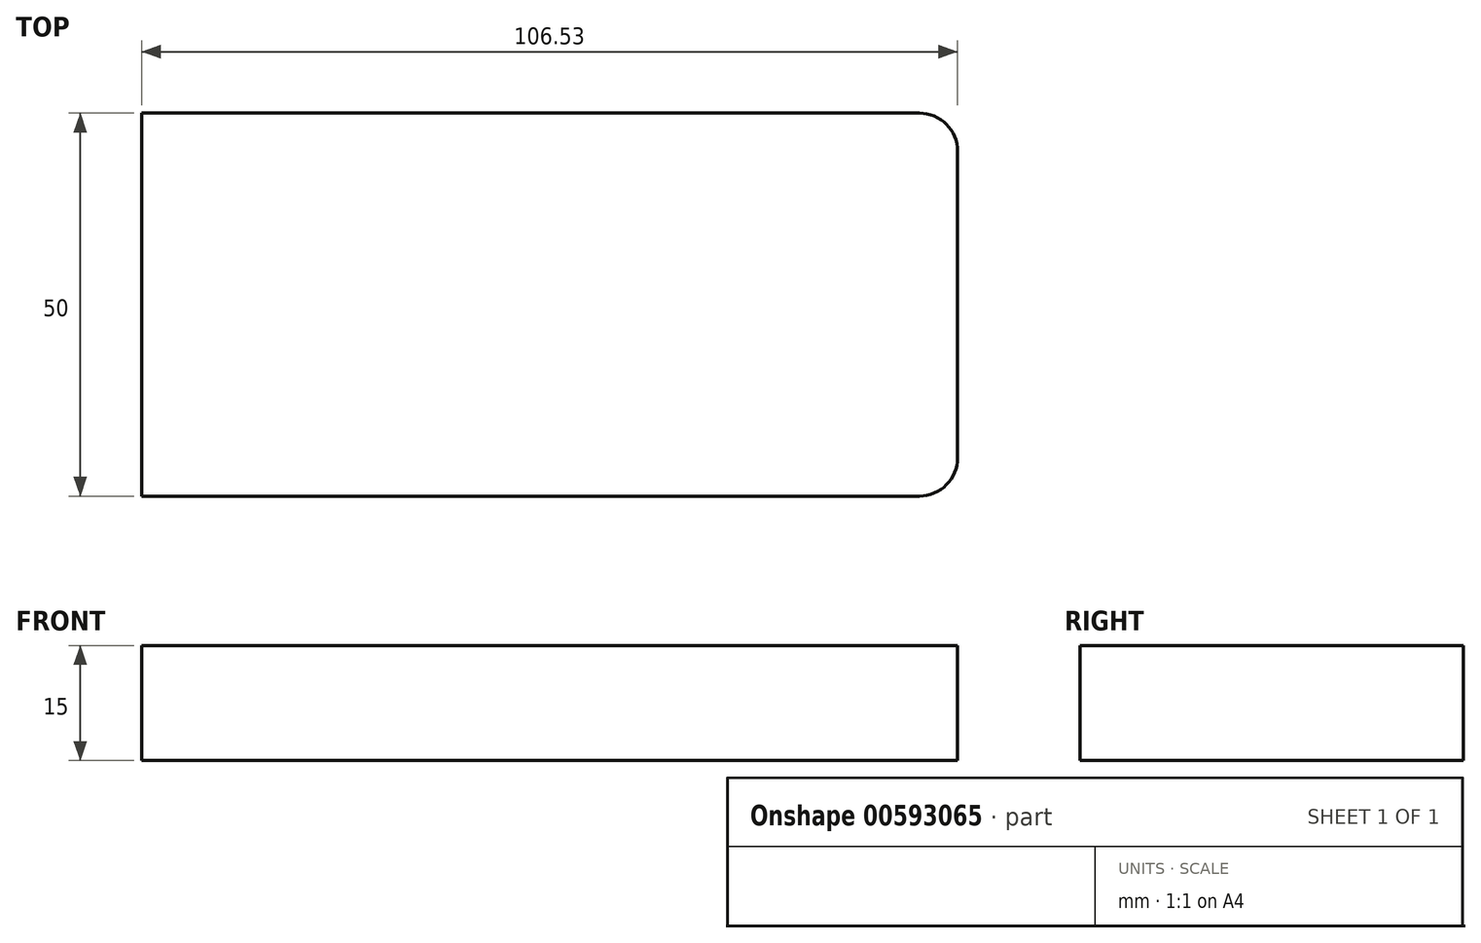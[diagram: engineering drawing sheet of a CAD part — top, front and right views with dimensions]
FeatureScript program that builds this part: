
annotation { "Feature Type Name" : "Feature", "Feature Type Description" : "" }
export const myFeature = defineFeature(function(context is Context, id is Id, definition is map)
    precondition{}
    {
        {
            var Q0;
            Q0=qCreatedBy(makeId("Top.planeOp"),FACE);
            var sketch = newSketch(context, id + "F0", { "sketchPlane" : qUnion([Q0])});
            skLineSegment(sketch, "E0.bottom", {"start": v(0, 0) * mm, "end": v(101.53, 0) * mm});
            skLineSegment(sketch, "E0.top", {"start": v(0, -50) * mm, "end": v(101.53, -50) * mm});
            skLineSegment(sketch, "E0.left", {"start": v(0, 0) * mm, "end": v(0, -50) * mm});
            skLineSegment(sketch, "E0.right", {"start": v(106.53, -5) * mm, "end": v(106.53, -45) * mm});
            skPoint(sketch, "E1.visualSharp", {"position": v(106.53, 0) * mm});
            skArc(sketch, "E1.filletArc", {"start": v(106.53, -5) * mm, "mid": v(105.06, -1.46) * mm, "end": v(101.53, 0) * mm});
            skPoint(sketch, "E2.visualSharp", {"position": v(106.53, -50) * mm});
            skArc(sketch, "E2.filletArc", {"start": v(101.53, -50) * mm, "mid": v(105.06, -48.54) * mm, "end": v(106.53, -45) * mm});
            skSolve(sketch);
        }
        {
            var Q0;
            Q0 = qSketchRegion(id + "F0", true);
            extrude(context, id + "F1", {"entities" : qUnion([Q0]), "depth" : 15 * mm, "offsetDistance" : 25 * mm});
        }
    });
